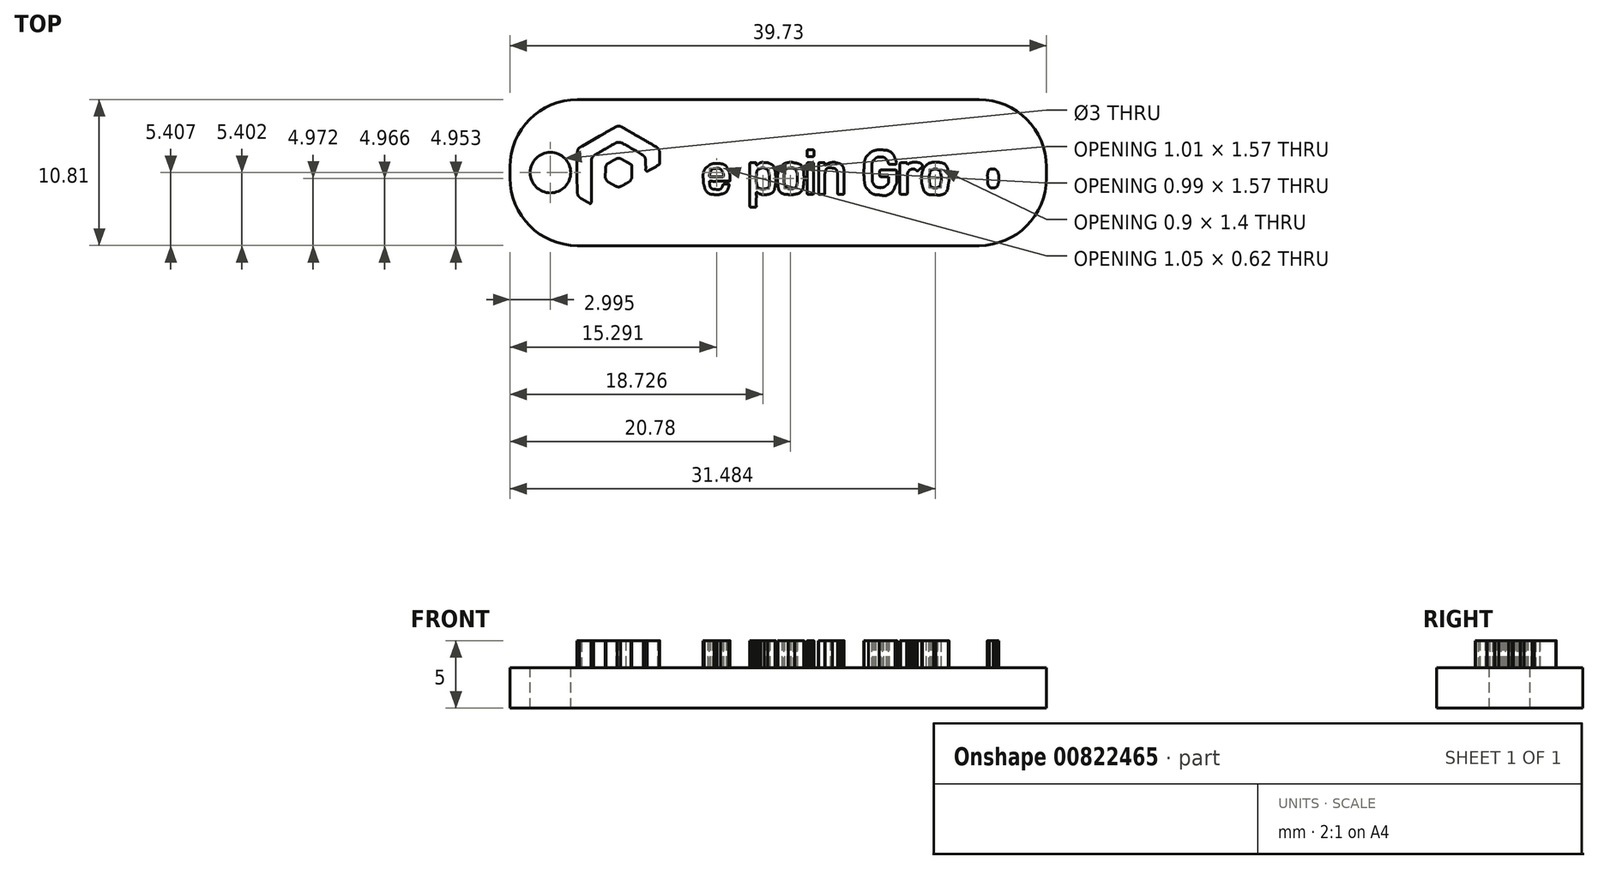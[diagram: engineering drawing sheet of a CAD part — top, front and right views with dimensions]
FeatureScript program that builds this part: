
annotation { "Feature Type Name" : "Feature", "Feature Type Description" : "" }
export const myFeature = defineFeature(function(context is Context, id is Id, definition is map)
    precondition{}
    {
        {
            var Q0;
            Q0=qCreatedBy(makeId("Top.planeOp"),FACE);
            var sketch = newSketch(context, id + "F0", { "sketchPlane" : qUnion([Q0])});
            skFitSpline(sketch, "E0", {"points": [v(-12.93, -3.42) * mm, v(-13.02, -3.4) * mm, v(-12.98, -3.42) * mm, v(-13.42, -3.17) * mm]});
            skFitSpline(sketch, "E1", {"points": [v(-13.42, -3.17) * mm, v(-13.69, -3.02) * mm, v(-13.79, -2.96) * mm, v(-13.8, -2.93) * mm]});
            skFitSpline(sketch, "E2", {"points": [v(-13.8, -2.93) * mm, v(-13.8, -2.9) * mm, v(-13.81, -2.8) * mm, v(-13.81, -2.4) * mm]});
            skFitSpline(sketch, "E3", {"points": [v(-13.81, -2.4) * mm, v(-13.81, -1.9) * mm, v(-13.81, -1.88) * mm, v(-13.77, -1.85) * mm]});
            skFitSpline(sketch, "E4", {"points": [v(-13.77, -1.85) * mm, v(-13.72, -1.82) * mm, v(-13.68, -1.83) * mm, v(-13.36, -2.02) * mm]});
            skFitSpline(sketch, "E5", {"points": [v(-13.36, -2.02) * mm, v(-13.19, -2.12) * mm, v(-13.02, -2.2) * mm, v(-12.98, -2.22) * mm]});
            skFitSpline(sketch, "E6", {"points": [v(-12.98, -2.22) * mm, v(-12.9, -2.25) * mm, v(-12.78, -2.25) * mm, v(-12.7, -2.23) * mm]});
            skFitSpline(sketch, "E7", {"points": [v(-12.7, -2.23) * mm, v(-12.65, -2.21) * mm, v(-12.17, -1.94) * mm, v(-11.38, -1.48) * mm]});
            skFitSpline(sketch, "E8", {"points": [v(-11.38, -1.48) * mm, v(-9.77, -0.55) * mm, v(-9.91, -0.63) * mm, v(-9.87, -0.64) * mm]});
            skFitSpline(sketch, "E9", {"points": [v(-9.87, -0.64) * mm, v(-9.85, -0.65) * mm, v(-9.82, -0.66) * mm, v(-9.81, -0.68) * mm]});
            skFitSpline(sketch, "E10", {"points": [v(-9.81, -0.68) * mm, v(-9.8, -0.7) * mm, v(-9.79, -0.72) * mm, v(-9.79, -1.13) * mm]});
            skFitSpline(sketch, "E11", {"points": [v(-9.79, -1.13) * mm, v(-9.79, -1.5) * mm, v(-9.8, -1.55) * mm, v(-9.81, -1.61) * mm]});
            skFitSpline(sketch, "E12", {"points": [v(-9.81, -1.61) * mm, v(-9.84, -1.7) * mm, v(-9.88, -1.77) * mm, v(-9.95, -1.84) * mm]});
            skFitSpline(sketch, "E13", {"points": [v(-9.95, -1.84) * mm, v(-10.01, -1.9) * mm, v(-12.57, -3.37) * mm, v(-12.66, -3.4) * mm]});
            skFitSpline(sketch, "E14", {"points": [v(-12.66, -3.4) * mm, v(-12.74, -3.43) * mm, v(-12.85, -3.44) * mm, v(-12.93, -3.42) * mm]});
            skFitSpline(sketch, "E15", {"points": [v(-3.1, -2.53) * mm, v(-3.1, -2.5) * mm, v(-3.11, -2.34) * mm, v(-3.11, -0.91) * mm]});
            skFitSpline(sketch, "E16", {"points": [v(-3.11, -0.91) * mm, v(-3.11, 0.5) * mm, v(-3.1, 0.68) * mm, v(-3.1, 0.7) * mm]});
            skFitSpline(sketch, "E17", {"points": [v(-3.1, 0.7) * mm, v(-3.08, 0.73) * mm, v(-3.07, 0.73) * mm, v(-2.88, 0.73) * mm]});
            skFitSpline(sketch, "E18", {"points": [v(-2.88, 0.73) * mm, v(-2.65, 0.73) * mm, v(-2.64, 0.73) * mm, v(-2.64, 0.63) * mm]});
            skFitSpline(sketch, "E19", {"points": [v(-2.64, 0.63) * mm, v(-2.64, 0.59) * mm, v(-2.63, 0.58) * mm, v(-2.6, 0.57) * mm]});
            skFitSpline(sketch, "E20", {"points": [v(-2.6, 0.57) * mm, v(-2.58, 0.56) * mm, v(-2.57, 0.57) * mm, v(-2.5, 0.61) * mm]});
            skFitSpline(sketch, "E21", {"points": [v(-2.5, 0.61) * mm, v(-2.36, 0.72) * mm, v(-2.22, 0.76) * mm, v(-1.99, 0.75) * mm]});
            skFitSpline(sketch, "E22", {"points": [v(-1.99, 0.75) * mm, v(-1.82, 0.74) * mm, v(-1.75, 0.73) * mm, v(-1.62, 0.67) * mm]});
            skFitSpline(sketch, "E23", {"points": [v(-1.62, 0.67) * mm, v(-1.46, 0.59) * mm, v(-1.33, 0.41) * mm, v(-1.26, 0.2) * mm]});
            skFitSpline(sketch, "E24", {"points": [v(-1.26, 0.2) * mm, v(-1.22, 0.05) * mm, v(-1.2, -0.06) * mm, v(-1.2, -0.36) * mm]});
            skFitSpline(sketch, "E25", {"points": [v(-1.2, -0.36) * mm, v(-1.2, -0.68) * mm, v(-1.2, -0.84) * mm, v(-1.25, -1.02) * mm]});
            skFitSpline(sketch, "E26", {"points": [v(-1.25, -1.02) * mm, v(-1.32, -1.34) * mm, v(-1.5, -1.53) * mm, v(-1.78, -1.6) * mm]});
            skFitSpline(sketch, "E27", {"points": [v(-1.78, -1.6) * mm, v(-1.83, -1.62) * mm, v(-1.9, -1.63) * mm, v(-2.03, -1.63) * mm]});
            skFitSpline(sketch, "E28", {"points": [v(-2.03, -1.63) * mm, v(-2.19, -1.63) * mm, v(-2.22, -1.63) * mm, v(-2.3, -1.6) * mm]});
            skFitSpline(sketch, "E29", {"points": [v(-2.3, -1.6) * mm, v(-2.38, -1.58) * mm, v(-2.45, -1.54) * mm, v(-2.52, -1.49) * mm]});
            skFitSpline(sketch, "E30", {"points": [v(-2.52, -1.49) * mm, v(-2.56, -1.45) * mm, v(-2.6, -1.45) * mm, v(-2.62, -1.47) * mm]});
            skFitSpline(sketch, "E31", {"points": [v(-2.62, -1.47) * mm, v(-2.63, -1.48) * mm, v(-2.63, -1.61) * mm, v(-2.63, -2) * mm]});
            skFitSpline(sketch, "E32", {"points": [v(-2.63, -2) * mm, v(-2.63, -2.44) * mm, v(-2.63, -2.5) * mm, v(-2.65, -2.53) * mm]});
            skFitSpline(sketch, "E33", {"points": [v(-2.65, -2.53) * mm, v(-2.66, -2.55) * mm, v(-2.67, -2.55) * mm, v(-2.87, -2.55) * mm]});
            skFitSpline(sketch, "E34", {"points": [v(-2.87, -2.55) * mm, v(-3.07, -2.55) * mm, v(-3.08, -2.55) * mm, v(-3.1, -2.53) * mm]});
            skFitSpline(sketch, "E35", {"points": [v(-2, -1.2) * mm, v(-1.75, -1.12) * mm, v(-1.65, -0.87) * mm, v(-1.67, -0.35) * mm]});
            skFitSpline(sketch, "E36", {"points": [v(-1.67, -0.35) * mm, v(-1.68, -0.14) * mm, v(-1.7, -0.02) * mm, v(-1.75, 0.1) * mm]});
            skFitSpline(sketch, "E37", {"points": [v(-1.75, 0.1) * mm, v(-1.79, 0.18) * mm, v(-1.86, 0.26) * mm, v(-1.94, 0.3) * mm]});
            skFitSpline(sketch, "E38", {"points": [v(-1.94, 0.3) * mm, v(-2.05, 0.34) * mm, v(-2.24, 0.34) * mm, v(-2.36, 0.3) * mm]});
            skFitSpline(sketch, "E39", {"points": [v(-2.36, 0.3) * mm, v(-2.5, 0.23) * mm, v(-2.59, 0.08) * mm, v(-2.62, -0.17) * mm]});
            skFitSpline(sketch, "E40", {"points": [v(-2.62, -0.17) * mm, v(-2.64, -0.32) * mm, v(-2.63, -0.71) * mm, v(-2.6, -0.82) * mm]});
            skFitSpline(sketch, "E41", {"points": [v(-2.6, -0.82) * mm, v(-2.56, -1.01) * mm, v(-2.46, -1.14) * mm, v(-2.32, -1.19) * mm]});
            skFitSpline(sketch, "E42", {"points": [v(-2.32, -1.19) * mm, v(-2.24, -1.21) * mm, v(-2.08, -1.22) * mm, v(-2, -1.2) * mm]});
            skFitSpline(sketch, "E43", {"points": [v(13.97, -2.53) * mm, v(13.96, -2.52) * mm, v(13.94, -2.5) * mm, v(13.93, -2.49) * mm]});
            skFitSpline(sketch, "E44", {"points": [v(13.93, -2.49) * mm, v(13.91, -2.46) * mm, v(13.9, -2.33) * mm, v(13.9, -0.9) * mm]});
            skFitSpline(sketch, "E45", {"points": [v(13.9, -0.9) * mm, v(13.9, 0.8) * mm, v(13.9, 0.7) * mm, v(13.97, 0.74) * mm]});
            skFitSpline(sketch, "E46", {"points": [v(13.97, 0.74) * mm, v(13.99, 0.75) * mm, v(14.07, 0.75) * mm, v(14.2, 0.75) * mm]});
            skFitSpline(sketch, "E47", {"points": [v(14.44, 0.72) * mm, v(14.46, 0.7) * mm, v(14.47, 0.68) * mm, v(14.47, 0.64) * mm]});
            skLineSegment(sketch, "E48", {"start": v(14.2, 0.75) * mm, "end": v(14.4, 0.75) * mm});
            skLineSegment(sketch, "E49", {"start": v(14.4, 0.75) * mm, "end": v(14.44, 0.72) * mm});
            skFitSpline(sketch, "E50", {"points": [v(14.52, 0.63) * mm, v(14.6, 0.69) * mm, v(14.68, 0.73) * mm, v(14.79, 0.75) * mm]});
            skFitSpline(sketch, "E51", {"points": [v(14.79, 0.75) * mm, v(14.91, 0.78) * mm, v(15.17, 0.78) * mm, v(15.3, 0.74) * mm]});
            skFitSpline(sketch, "E52", {"points": [v(15.3, 0.74) * mm, v(15.63, 0.63) * mm, v(15.8, 0.4) * mm, v(15.86, -0.05) * mm]});
            skFitSpline(sketch, "E53", {"points": [v(15.86, -0.05) * mm, v(15.88, -0.2) * mm, v(15.88, -0.7) * mm, v(15.86, -0.86) * mm]});
            skFitSpline(sketch, "E54", {"points": [v(15.86, -0.86) * mm, v(15.79, -1.3) * mm, v(15.6, -1.53) * mm, v(15.26, -1.63) * mm]});
            skFitSpline(sketch, "E55", {"points": [v(15.26, -1.63) * mm, v(15.19, -1.64) * mm, v(15.14, -1.65) * mm, v(15.01, -1.65) * mm]});
            skFitSpline(sketch, "E56", {"points": [v(15.01, -1.65) * mm, v(14.8, -1.65) * mm, v(14.67, -1.62) * mm, v(14.53, -1.52) * mm]});
            skLineSegment(sketch, "E57", {"start": v(14.47, 0.64) * mm, "end": v(14.47, 0.6) * mm});
            skLineSegment(sketch, "E58", {"start": v(14.47, 0.6) * mm, "end": v(14.52, 0.63) * mm});
            skFitSpline(sketch, "E59", {"points": [v(14.48, -1.97) * mm, v(14.48, -2.5) * mm, v(14.48, -2.5) * mm, v(14.42, -2.53) * mm]});
            skFitSpline(sketch, "E60", {"points": [v(14.42, -2.53) * mm, v(14.38, -2.55) * mm, v(14, -2.55) * mm, v(13.97, -2.53) * mm]});
            skLineSegment(sketch, "E61", {"start": v(14.53, -1.52) * mm, "end": v(14.48, -1.48) * mm});
            skLineSegment(sketch, "E62", {"start": v(14.48, -1.48) * mm, "end": v(14.48, -1.97) * mm});
            skFitSpline(sketch, "E63", {"points": [v(15.08, -1.1) * mm, v(15.18, -1.06) * mm, v(15.24, -0.97) * mm, v(15.28, -0.8) * mm]});
            skFitSpline(sketch, "E64", {"points": [v(15.28, -0.8) * mm, v(15.31, -0.7) * mm, v(15.31, -0.17) * mm, v(15.28, -0.07) * mm]});
            skFitSpline(sketch, "E65", {"points": [v(15.28, -0.07) * mm, v(15.25, 0.05) * mm, v(15.22, 0.1) * mm, v(15.16, 0.17) * mm]});
            skFitSpline(sketch, "E66", {"points": [v(15.16, 0.17) * mm, v(15.08, 0.24) * mm, v(15, 0.26) * mm, v(14.87, 0.26) * mm]});
            skFitSpline(sketch, "E67", {"points": [v(14.87, 0.26) * mm, v(14.67, 0.25) * mm, v(14.56, 0.15) * mm, v(14.5, -0.07) * mm]});
            skFitSpline(sketch, "E68", {"points": [v(14.5, -0.07) * mm, v(14.49, -0.14) * mm, v(14.49, -0.2) * mm, v(14.49, -0.44) * mm]});
            skFitSpline(sketch, "E69", {"points": [v(14.49, -0.44) * mm, v(14.49, -0.7) * mm, v(14.49, -0.74) * mm, v(14.51, -0.82) * mm]});
            skFitSpline(sketch, "E70", {"points": [v(14.51, -0.82) * mm, v(14.54, -0.93) * mm, v(14.58, -1) * mm, v(14.64, -1.05) * mm]});
            skFitSpline(sketch, "E71", {"points": [v(14.64, -1.05) * mm, v(14.71, -1.11) * mm, v(14.78, -1.13) * mm, v(14.91, -1.13) * mm]});
            skFitSpline(sketch, "E72", {"points": [v(14.91, -1.13) * mm, v(15, -1.13) * mm, v(15.04, -1.12) * mm, v(15.07, -1.1) * mm]});
            skFitSpline(sketch, "E73", {"points": [v(-15.32, -2.08) * mm, v(-15.58, -1.93) * mm, v(-15.67, -1.87) * mm, v(-15.72, -1.82) * mm]});
            skFitSpline(sketch, "E74", {"points": [v(-15.72, -1.82) * mm, v(-15.8, -1.75) * mm, v(-15.84, -1.67) * mm, v(-15.86, -1.57) * mm]});
            skFitSpline(sketch, "E75", {"points": [v(-15.86, -1.57) * mm, v(-15.88, -1.49) * mm, v(-15.88, 1.49) * mm, v(-15.86, 1.57) * mm]});
            skFitSpline(sketch, "E76", {"points": [v(-15.86, 1.57) * mm, v(-15.83, 1.73) * mm, v(-15.74, 1.84) * mm, v(-15.53, 1.95) * mm]});
            skFitSpline(sketch, "E77", {"points": [v(-15.53, 1.95) * mm, v(-15.46, 2) * mm, v(-14.87, 2.34) * mm, v(-14.22, 2.71) * mm]});
            skFitSpline(sketch, "E78", {"points": [v(-14.22, 2.71) * mm, v(-13.57, 3.08) * mm, v(-13.02, 3.4) * mm, v(-12.98, 3.41) * mm]});
            skFitSpline(sketch, "E79", {"points": [v(-12.98, 3.41) * mm, v(-12.9, 3.44) * mm, v(-12.75, 3.44) * mm, v(-12.67, 3.4) * mm]});
            skFitSpline(sketch, "E80", {"points": [v(-12.67, 3.4) * mm, v(-12.63, 3.4) * mm, v(-12.02, 3.05) * mm, v(-11.3, 2.64) * mm]});
            skFitSpline(sketch, "E81", {"points": [v(-11.3, 2.64) * mm, v(-10.33, 2.07) * mm, v(-10, 1.87) * mm, v(-9.94, 1.83) * mm]});
            skFitSpline(sketch, "E82", {"points": [v(-9.94, 1.83) * mm, v(-9.9, 1.79) * mm, v(-9.87, 1.74) * mm, v(-9.84, 1.68) * mm]});
            skFitSpline(sketch, "E83", {"points": [v(-9.8, 1.12) * mm, v(-9.79, 0.67) * mm, v(-9.79, 0.64) * mm, v(-9.8, 0.62) * mm]});
            skFitSpline(sketch, "E84", {"points": [v(-9.8, 0.62) * mm, v(-9.84, 0.6) * mm, v(-10.69, 0.1) * mm, v(-10.71, 0.1) * mm]});
            skFitSpline(sketch, "E85", {"points": [v(-10.71, 0.1) * mm, v(-10.75, 0.1) * mm, v(-10.79, 0.13) * mm, v(-10.8, 0.16) * mm]});
            skFitSpline(sketch, "E86", {"points": [v(-10.8, 0.16) * mm, v(-10.82, 0.18) * mm, v(-10.82, 0.26) * mm, v(-10.82, 0.57) * mm]});
            skFitSpline(sketch, "E87", {"points": [v(-10.82, 0.57) * mm, v(-10.82, 0.91) * mm, v(-10.82, 0.96) * mm, v(-10.84, 1.02) * mm]});
            skFitSpline(sketch, "E88", {"points": [v(-10.84, 1.02) * mm, v(-10.87, 1.1) * mm, v(-10.92, 1.19) * mm, v(-10.98, 1.24) * mm]});
            skFitSpline(sketch, "E89", {"points": [v(-10.98, 1.24) * mm, v(-11.06, 1.3) * mm, v(-12.62, 2.2) * mm, v(-12.7, 2.23) * mm]});
            skFitSpline(sketch, "E90", {"points": [v(-12.7, 2.23) * mm, v(-12.74, 2.24) * mm, v(-12.8, 2.24) * mm, v(-12.86, 2.24) * mm]});
            skFitSpline(sketch, "E91", {"points": [v(-12.86, 2.24) * mm, v(-12.94, 2.24) * mm, v(-12.97, 2.23) * mm, v(-13.04, 2.2) * mm]});
            skFitSpline(sketch, "E92", {"points": [v(-13.04, 2.2) * mm, v(-13.09, 2.17) * mm, v(-13.46, 1.96) * mm, v(-13.88, 1.72) * mm]});
            skFitSpline(sketch, "E93", {"points": [v(-13.88, 1.72) * mm, v(-14.46, 1.38) * mm, v(-14.65, 1.27) * mm, v(-14.7, 1.22) * mm]});
            skFitSpline(sketch, "E94", {"points": [v(-14.7, 1.22) * mm, v(-14.76, 1.16) * mm, v(-14.82, 1.06) * mm, v(-14.83, 0.97) * mm]});
            skFitSpline(sketch, "E95", {"points": [v(-14.83, 0.97) * mm, v(-14.84, 0.93) * mm, v(-14.84, 0.34) * mm, v(-14.84, -0.66) * mm]});
            skLineSegment(sketch, "E96", {"start": v(-9.84, 1.68) * mm, "end": v(-9.8, 1.6) * mm});
            skLineSegment(sketch, "E97", {"start": v(-9.8, 1.6) * mm, "end": v(-9.8, 1.12) * mm});
            skFitSpline(sketch, "E98", {"points": [v(-14.87, -2.25) * mm, v(-14.93, -2.3) * mm, v(-14.95, -2.3) * mm, v(-15.32, -2.08) * mm]});
            skLineSegment(sketch, "E99", {"start": v(-14.84, -0.66) * mm, "end": v(-14.84, -2.22) * mm});
            skLineSegment(sketch, "E100", {"start": v(-14.84, -2.22) * mm, "end": v(-14.87, -2.25) * mm});
            skFitSpline(sketch, "E101", {"points": [v(6.45, -1.65) * mm, v(6.13, -1.62) * mm, v(5.88, -1.5) * mm, v(5.67, -1.3) * mm]});
            skFitSpline(sketch, "E102", {"points": [v(5.67, -1.3) * mm, v(5.5, -1.1) * mm, v(5.4, -0.9) * mm, v(5.37, -0.6) * mm]});
            skFitSpline(sketch, "E103", {"points": [v(5.37, -0.6) * mm, v(5.35, -0.43) * mm, v(5.35, 0.46) * mm, v(5.37, 0.63) * mm]});
            skFitSpline(sketch, "E104", {"points": [v(5.37, 0.63) * mm, v(5.4, 0.95) * mm, v(5.5, 1.17) * mm, v(5.7, 1.36) * mm]});
            skFitSpline(sketch, "E105", {"points": [v(5.7, 1.36) * mm, v(5.84, 1.5) * mm, v(6.01, 1.6) * mm, v(6.22, 1.65) * mm]});
            skFitSpline(sketch, "E106", {"points": [v(6.22, 1.65) * mm, v(6.37, 1.7) * mm, v(6.62, 1.7) * mm, v(6.78, 1.68) * mm]});
            skFitSpline(sketch, "E107", {"points": [v(6.78, 1.68) * mm, v(7.18, 1.6) * mm, v(7.47, 1.4) * mm, v(7.64, 1.05) * mm]});
            skFitSpline(sketch, "E108", {"points": [v(7.64, 1.05) * mm, v(7.67, 0.98) * mm, v(7.71, 0.88) * mm, v(7.73, 0.82) * mm]});
            skFitSpline(sketch, "E109", {"points": [v(7.73, 0.82) * mm, v(7.76, 0.72) * mm, v(7.76, 0.7) * mm, v(7.74, 0.67) * mm]});
            skFitSpline(sketch, "E110", {"points": [v(7.74, 0.67) * mm, v(7.73, 0.65) * mm, v(7.72, 0.62) * mm, v(7.7, 0.62) * mm]});
            skFitSpline(sketch, "E111", {"points": [v(7.7, 0.62) * mm, v(7.69, 0.61) * mm, v(7.6, 0.6) * mm, v(7.45, 0.6) * mm]});
            skFitSpline(sketch, "E112", {"points": [v(7.45, 0.6) * mm, v(7.27, 0.6) * mm, v(7.22, 0.6) * mm, v(7.2, 0.62) * mm]});
            skFitSpline(sketch, "E113", {"points": [v(7.2, 0.62) * mm, v(7.19, 0.63) * mm, v(7.16, 0.68) * mm, v(7.15, 0.73) * mm]});
            skFitSpline(sketch, "E114", {"points": [v(7.15, 0.73) * mm, v(7.1, 0.84) * mm, v(7.05, 0.92) * mm, v(6.98, 1) * mm]});
            skFitSpline(sketch, "E115", {"points": [v(6.98, 1) * mm, v(6.86, 1.11) * mm, v(6.7, 1.16) * mm, v(6.52, 1.15) * mm]});
            skFitSpline(sketch, "E116", {"points": [v(6.52, 1.15) * mm, v(6.36, 1.14) * mm, v(6.24, 1.09) * mm, v(6.13, 0.99) * mm]});
            skFitSpline(sketch, "E117", {"points": [v(6.13, 0.99) * mm, v(5.98, 0.83) * mm, v(5.93, 0.58) * mm, v(5.95, -0.1) * mm]});
            skFitSpline(sketch, "E118", {"points": [v(5.95, -0.1) * mm, v(5.95, -0.56) * mm, v(5.97, -0.69) * mm, v(6.06, -0.85) * mm]});
            skFitSpline(sketch, "E119", {"points": [v(6.06, -0.85) * mm, v(6.12, -0.96) * mm, v(6.25, -1.06) * mm, v(6.4, -1.1) * mm]});
            skFitSpline(sketch, "E120", {"points": [v(6.4, -1.1) * mm, v(6.46, -1.11) * mm, v(6.62, -1.11) * mm, v(6.7, -1.1) * mm]});
            skFitSpline(sketch, "E121", {"points": [v(6.7, -1.1) * mm, v(6.8, -1.08) * mm, v(6.93, -1.01) * mm, v(7, -0.94) * mm]});
            skFitSpline(sketch, "E122", {"points": [v(7, -0.94) * mm, v(7.13, -0.8) * mm, v(7.17, -0.67) * mm, v(7.17, -0.45) * mm]});
            skFitSpline(sketch, "E123", {"points": [v(7.77, -0.2) * mm, v(7.77, -0.67) * mm, v(7.75, -0.8) * mm, v(7.64, -1.02) * mm]});
            skFitSpline(sketch, "E124", {"points": [v(7.64, -1.02) * mm, v(7.44, -1.44) * mm, v(6.97, -1.7) * mm, v(6.45, -1.65) * mm]});
            skLineSegment(sketch, "E125", {"start": v(7.17, -0.45) * mm, "end": v(7.17, -0.31) * mm});
            skLineSegment(sketch, "E126", {"start": v(7.17, -0.31) * mm, "end": v(6.87, -0.31) * mm});
            skLineSegment(sketch, "E127", {"start": v(6.87, -0.31) * mm, "end": v(6.57, -0.31) * mm});
            skLineSegment(sketch, "E128", {"start": v(6.57, -0.31) * mm, "end": v(6.54, -0.28) * mm});
            skLineSegment(sketch, "E129", {"start": v(6.54, -0.28) * mm, "end": v(6.5, -0.26) * mm});
            skLineSegment(sketch, "E130", {"start": v(6.5, -0.26) * mm, "end": v(6.5, -0.06) * mm});
            skLineSegment(sketch, "E131", {"start": v(6.5, -0.06) * mm, "end": v(6.5, 0.14) * mm});
            skLineSegment(sketch, "E132", {"start": v(6.5, 0.14) * mm, "end": v(6.53, 0.17) * mm});
            skLineSegment(sketch, "E133", {"start": v(6.53, 0.17) * mm, "end": v(6.56, 0.2) * mm});
            skLineSegment(sketch, "E134", {"start": v(6.56, 0.2) * mm, "end": v(7.14, 0.2) * mm});
            skLineSegment(sketch, "E135", {"start": v(7.14, 0.2) * mm, "end": v(7.7, 0.2) * mm});
            skLineSegment(sketch, "E136", {"start": v(7.7, 0.2) * mm, "end": v(7.74, 0.17) * mm});
            skLineSegment(sketch, "E137", {"start": v(7.74, 0.17) * mm, "end": v(7.77, 0.14) * mm});
            skLineSegment(sketch, "E138", {"start": v(7.77, 0.14) * mm, "end": v(7.77, -0.2) * mm});
            skFitSpline(sketch, "E139", {"points": [v(10.49, -1.65) * mm, v(10.09, -1.6) * mm, v(9.8, -1.36) * mm, v(9.68, -0.99) * mm]});
            skFitSpline(sketch, "E140", {"points": [v(9.68, -0.99) * mm, v(9.63, -0.83) * mm, v(9.61, -0.66) * mm, v(9.62, -0.37) * mm]});
            skFitSpline(sketch, "E141", {"points": [v(9.62, -0.37) * mm, v(9.63, -0.1) * mm, v(9.64, 0.02) * mm, v(9.7, 0.17) * mm]});
            skFitSpline(sketch, "E142", {"points": [v(9.7, 0.17) * mm, v(9.75, 0.31) * mm, v(9.8, 0.39) * mm, v(9.91, 0.5) * mm]});
            skFitSpline(sketch, "E143", {"points": [v(9.91, 0.5) * mm, v(10.05, 0.63) * mm, v(10.16, 0.7) * mm, v(10.34, 0.75) * mm]});
            skFitSpline(sketch, "E144", {"points": [v(10.34, 0.75) * mm, v(10.43, 0.77) * mm, v(10.7, 0.78) * mm, v(10.8, 0.76) * mm]});
            skFitSpline(sketch, "E145", {"points": [v(10.8, 0.76) * mm, v(11.2, 0.7) * mm, v(11.49, 0.42) * mm, v(11.58, 0) * mm]});
            skFitSpline(sketch, "E146", {"points": [v(11.58, 0) * mm, v(11.63, -0.21) * mm, v(11.63, -0.66) * mm, v(11.58, -0.88) * mm]});
            skFitSpline(sketch, "E147", {"points": [v(11.58, -0.88) * mm, v(11.48, -1.35) * mm, v(11.15, -1.62) * mm, v(10.66, -1.65) * mm]});
            skFitSpline(sketch, "E148", {"points": [v(10.66, -1.65) * mm, v(10.6, -1.65) * mm, v(10.53, -1.65) * mm, v(10.49, -1.65) * mm]});
            skFitSpline(sketch, "E149", {"points": [v(10.8, -1.1) * mm, v(10.91, -1.04) * mm, v(10.98, -0.95) * mm, v(11.03, -0.78) * mm]});
            skFitSpline(sketch, "E150", {"points": [v(11.03, -0.78) * mm, v(11.05, -0.67) * mm, v(11.05, -0.2) * mm, v(11.03, -0.1) * mm]});
            skFitSpline(sketch, "E151", {"points": [v(11.03, -0.1) * mm, v(10.98, 0.07) * mm, v(10.92, 0.17) * mm, v(10.8, 0.22) * mm]});
            skFitSpline(sketch, "E152", {"points": [v(10.8, 0.22) * mm, v(10.74, 0.25) * mm, v(10.72, 0.25) * mm, v(10.61, 0.25) * mm]});
            skFitSpline(sketch, "E153", {"points": [v(10.61, 0.25) * mm, v(10.51, 0.25) * mm, v(10.49, 0.25) * mm, v(10.43, 0.22) * mm]});
            skFitSpline(sketch, "E154", {"points": [v(10.43, 0.22) * mm, v(10.32, 0.17) * mm, v(10.25, 0.07) * mm, v(10.21, -0.07) * mm]});
            skFitSpline(sketch, "E155", {"points": [v(10.21, -0.07) * mm, v(10.18, -0.22) * mm, v(10.17, -0.58) * mm, v(10.2, -0.76) * mm]});
            skFitSpline(sketch, "E156", {"points": [v(10.2, -0.76) * mm, v(10.24, -0.93) * mm, v(10.33, -1.06) * mm, v(10.46, -1.1) * mm]});
            skFitSpline(sketch, "E157", {"points": [v(10.46, -1.1) * mm, v(10.55, -1.14) * mm, v(10.7, -1.14) * mm, v(10.8, -1.1) * mm]});
            skFitSpline(sketch, "E158", {"points": [v(12.5, -1.65) * mm, v(12.3, -1.62) * mm, v(12.15, -1.55) * mm, v(12.02, -1.42) * mm]});
            skFitSpline(sketch, "E159", {"points": [v(12.02, -1.42) * mm, v(11.89, -1.28) * mm, v(11.82, -1.13) * mm, v(11.8, -0.92) * mm]});
            skFitSpline(sketch, "E160", {"points": [v(11.8, -0.92) * mm, v(11.78, -0.86) * mm, v(11.78, -0.52) * mm, v(11.78, -0.08) * mm]});
            skFitSpline(sketch, "E161", {"points": [v(11.78, -0.08) * mm, v(11.78, 0.73) * mm, v(11.78, 0.7) * mm, v(11.84, 0.74) * mm]});
            skFitSpline(sketch, "E162", {"points": [v(11.84, 0.74) * mm, v(11.86, 0.75) * mm, v(11.94, 0.75) * mm, v(12.07, 0.75) * mm]});
            skFitSpline(sketch, "E163", {"points": [v(12.07, 0.75) * mm, v(12.27, 0.75) * mm, v(12.31, 0.74) * mm, v(12.34, 0.7) * mm]});
            skFitSpline(sketch, "E164", {"points": [v(12.34, 0.7) * mm, v(12.34, 0.69) * mm, v(12.35, 0.34) * mm, v(12.35, -0.08) * mm]});
            skFitSpline(sketch, "E165", {"points": [v(12.38, -0.9) * mm, v(12.42, -0.98) * mm, v(12.48, -1.06) * mm, v(12.56, -1.1) * mm]});
            skFitSpline(sketch, "E166", {"points": [v(12.56, -1.1) * mm, v(12.61, -1.12) * mm, v(12.63, -1.13) * mm, v(12.75, -1.13) * mm]});
            skFitSpline(sketch, "E167", {"points": [v(12.75, -1.13) * mm, v(12.87, -1.13) * mm, v(12.89, -1.12) * mm, v(12.95, -1.1) * mm]});
            skFitSpline(sketch, "E168", {"points": [v(12.95, -1.1) * mm, v(13.03, -1.06) * mm, v(13.1, -0.98) * mm, v(13.13, -0.9) * mm]});
            skFitSpline(sketch, "E169", {"points": [v(13.13, -0.9) * mm, v(13.15, -0.83) * mm, v(13.15, -0.83) * mm, v(13.16, -0.07) * mm]});
            skLineSegment(sketch, "E170", {"start": v(12.35, -0.08) * mm, "end": v(12.36, -0.83) * mm});
            skLineSegment(sketch, "E171", {"start": v(12.36, -0.83) * mm, "end": v(12.38, -0.9) * mm});
            skFitSpline(sketch, "E172", {"points": [v(13.45, -1.62) * mm, v(13.24, -1.62) * mm, v(13.24, -1.62) * mm, v(13.21, -1.6) * mm]});
            skFitSpline(sketch, "E173", {"points": [v(13.21, -1.6) * mm, v(13.2, -1.58) * mm, v(13.18, -1.55) * mm, v(13.17, -1.52) * mm]});
            skLineSegment(sketch, "E174", {"start": v(13.16, -0.07) * mm, "end": v(13.16, 0.69) * mm});
            skLineSegment(sketch, "E175", {"start": v(13.16, 0.69) * mm, "end": v(13.2, 0.72) * mm});
            skLineSegment(sketch, "E176", {"start": v(13.2, 0.72) * mm, "end": v(13.24, 0.75) * mm});
            skLineSegment(sketch, "E177", {"start": v(13.24, 0.75) * mm, "end": v(13.45, 0.75) * mm});
            skLineSegment(sketch, "E178", {"start": v(13.45, 0.75) * mm, "end": v(13.66, 0.75) * mm});
            skLineSegment(sketch, "E179", {"start": v(13.66, 0.75) * mm, "end": v(13.7, 0.72) * mm});
            skLineSegment(sketch, "E180", {"start": v(13.7, 0.72) * mm, "end": v(13.73, 0.69) * mm});
            skLineSegment(sketch, "E181", {"start": v(13.73, 0.69) * mm, "end": v(13.73, -0.44) * mm});
            skLineSegment(sketch, "E182", {"start": v(13.73, -0.44) * mm, "end": v(13.73, -1.56) * mm});
            skLineSegment(sketch, "E183", {"start": v(13.73, -1.56) * mm, "end": v(13.7, -1.6) * mm});
            skLineSegment(sketch, "E184", {"start": v(13.7, -1.6) * mm, "end": v(13.66, -1.62) * mm});
            skLineSegment(sketch, "E185", {"start": v(13.66, -1.62) * mm, "end": v(13.45, -1.62) * mm});
            skFitSpline(sketch, "E186", {"points": [v(13.13, -1.5) * mm, v(12.96, -1.61) * mm, v(12.71, -1.67) * mm, v(12.5, -1.65) * mm]});
            skLineSegment(sketch, "E187", {"start": v(13.17, -1.52) * mm, "end": v(13.17, -1.48) * mm});
            skLineSegment(sketch, "E188", {"start": v(13.17, -1.48) * mm, "end": v(13.13, -1.5) * mm});
            skFitSpline(sketch, "E189", {"points": [v(-5.76, -1.62) * mm, v(-6.11, -1.56) * mm, v(-6.37, -1.33) * mm, v(-6.49, -0.96) * mm]});
            skFitSpline(sketch, "E190", {"points": [v(-6.49, -0.96) * mm, v(-6.54, -0.8) * mm, v(-6.56, -0.66) * mm, v(-6.56, -0.47) * mm]});
            skFitSpline(sketch, "E191", {"points": [v(-6.56, -0.47) * mm, v(-6.56, -0.07) * mm, v(-6.45, 0.25) * mm, v(-6.22, 0.46) * mm]});
            skFitSpline(sketch, "E192", {"points": [v(-6.22, 0.46) * mm, v(-6.12, 0.55) * mm, v(-6.03, 0.6) * mm, v(-5.9, 0.65) * mm]});
            skFitSpline(sketch, "E193", {"points": [v(-5.9, 0.65) * mm, v(-5.79, 0.69) * mm, v(-5.78, 0.69) * mm, v(-5.57, 0.69) * mm]});
            skFitSpline(sketch, "E194", {"points": [v(-5.57, 0.69) * mm, v(-5.38, 0.69) * mm, v(-5.35, 0.69) * mm, v(-5.27, 0.66) * mm]});
            skFitSpline(sketch, "E195", {"points": [v(-5.27, 0.66) * mm, v(-5.02, 0.6) * mm, v(-4.84, 0.44) * mm, v(-4.72, 0.2) * mm]});
            skFitSpline(sketch, "E196", {"points": [v(-4.72, 0.2) * mm, v(-4.64, 0.02) * mm, v(-4.6, -0.17) * mm, v(-4.58, -0.43) * mm]});
            skFitSpline(sketch, "E197", {"points": [v(-4.58, -0.43) * mm, v(-4.58, -0.6) * mm, v(-4.58, -0.6) * mm, v(-4.6, -0.62) * mm]});
            skFitSpline(sketch, "E198", {"points": [v(-4.6, -0.62) * mm, v(-4.63, -0.64) * mm, v(-4.7, -0.64) * mm, v(-5.35, -0.64) * mm]});
            skFitSpline(sketch, "E199", {"points": [v(-5.35, -0.64) * mm, v(-5.98, -0.64) * mm, v(-6.07, -0.64) * mm, v(-6.08, -0.66) * mm]});
            skFitSpline(sketch, "E200", {"points": [v(-6.08, -0.66) * mm, v(-6.1, -0.67) * mm, v(-6.1, -0.7) * mm, v(-6.09, -0.75) * mm]});
            skFitSpline(sketch, "E201", {"points": [v(-6.09, -0.75) * mm, v(-6.06, -1.01) * mm, v(-5.9, -1.2) * mm, v(-5.65, -1.24) * mm]});
            skFitSpline(sketch, "E202", {"points": [v(-5.65, -1.24) * mm, v(-5.42, -1.27) * mm, v(-5.22, -1.16) * mm, v(-5.12, -0.96) * mm]});
            skFitSpline(sketch, "E203", {"points": [v(-5.12, -0.96) * mm, v(-5.1, -0.92) * mm, v(-5.08, -0.87) * mm, v(-5.06, -0.87) * mm]});
            skFitSpline(sketch, "E204", {"points": [v(-5.06, -0.87) * mm, v(-5.05, -0.86) * mm, v(-5, -0.85) * mm, v(-4.86, -0.85) * mm]});
            skFitSpline(sketch, "E205", {"points": [v(-4.86, -0.85) * mm, v(-4.7, -0.85) * mm, v(-4.67, -0.85) * mm, v(-4.65, -0.87) * mm]});
            skFitSpline(sketch, "E206", {"points": [v(-4.65, -0.87) * mm, v(-4.63, -0.9) * mm, v(-4.63, -0.93) * mm, v(-4.66, -1.02) * mm]});
            skFitSpline(sketch, "E207", {"points": [v(-4.66, -1.02) * mm, v(-4.78, -1.32) * mm, v(-4.98, -1.51) * mm, v(-5.27, -1.6) * mm]});
            skFitSpline(sketch, "E208", {"points": [v(-5.27, -1.6) * mm, v(-5.35, -1.62) * mm, v(-5.4, -1.63) * mm, v(-5.54, -1.63) * mm]});
            skFitSpline(sketch, "E209", {"points": [v(-5.54, -1.63) * mm, v(-5.63, -1.63) * mm, v(-5.73, -1.63) * mm, v(-5.76, -1.62) * mm]});
            skFitSpline(sketch, "E210", {"points": [v(-5.07, -0.28) * mm, v(-5.06, -0.26) * mm, v(-5.05, -0.24) * mm, v(-5.06, -0.18) * mm]});
            skFitSpline(sketch, "E211", {"points": [v(-5.06, -0.18) * mm, v(-5.08, -0.08) * mm, v(-5.09, -0.04) * mm, v(-5.14, 0.05) * mm]});
            skFitSpline(sketch, "E212", {"points": [v(-5.14, 0.05) * mm, v(-5.23, 0.22) * mm, v(-5.4, 0.31) * mm, v(-5.61, 0.3) * mm]});
            skFitSpline(sketch, "E213", {"points": [v(-5.61, 0.3) * mm, v(-5.82, 0.29) * mm, v(-5.98, 0.17) * mm, v(-6.05, -0.04) * mm]});
            skFitSpline(sketch, "E214", {"points": [v(-6.05, -0.04) * mm, v(-6.09, -0.13) * mm, v(-6.1, -0.26) * mm, v(-6.08, -0.28) * mm]});
            skFitSpline(sketch, "E215", {"points": [v(-6.08, -0.28) * mm, v(-6.07, -0.3) * mm, v(-6, -0.3) * mm, v(-5.58, -0.3) * mm]});
            skFitSpline(sketch, "E216", {"points": [v(-0.27, -1.62) * mm, v(-0.7, -1.55) * mm, v(-0.97, -1.25) * mm, v(-1.04, -0.77) * mm]});
            skFitSpline(sketch, "E217", {"points": [v(-1.04, -0.77) * mm, v(-1.06, -0.65) * mm, v(-1.06, -0.24) * mm, v(-1.04, -0.11) * mm]});
            skFitSpline(sketch, "E218", {"points": [v(-1.04, -0.11) * mm, v(-1, 0.15) * mm, v(-0.91, 0.36) * mm, v(-0.76, 0.5) * mm]});
            skFitSpline(sketch, "E219", {"points": [v(-0.76, 0.5) * mm, v(-0.63, 0.62) * mm, v(-0.47, 0.7) * mm, v(-0.3, 0.73) * mm]});
            skFitSpline(sketch, "E220", {"points": [v(-0.3, 0.73) * mm, v(-0.18, 0.76) * mm, v(0.08, 0.75) * mm, v(0.19, 0.72) * mm]});
            skFitSpline(sketch, "E221", {"points": [v(0.19, 0.72) * mm, v(0.59, 0.61) * mm, v(0.82, 0.33) * mm, v(0.88, -0.12) * mm]});
            skFitSpline(sketch, "E222", {"points": [v(0.88, -0.12) * mm, v(0.9, -0.27) * mm, v(0.9, -0.65) * mm, v(0.87, -0.8) * mm]});
            skFitSpline(sketch, "E223", {"points": [v(0.87, -0.8) * mm, v(0.8, -1.22) * mm, v(0.57, -1.5) * mm, v(0.2, -1.6) * mm]});
            skFitSpline(sketch, "E224", {"points": [v(0.2, -1.6) * mm, v(0.1, -1.63) * mm, v(-0.17, -1.64) * mm, v(-0.27, -1.62) * mm]});
            skLineSegment(sketch, "E225", {"start": v(-5.58, -0.3) * mm, "end": v(-5.08, -0.3) * mm});
            skLineSegment(sketch, "E226", {"start": v(-5.08, -0.3) * mm, "end": v(-5.07, -0.28) * mm});
            skFitSpline(sketch, "E227", {"points": [v(0.13, -1.17) * mm, v(0.27, -1.1) * mm, v(0.35, -0.99) * mm, v(0.4, -0.8) * mm]});
            skFitSpline(sketch, "E228", {"points": [v(0.4, -0.8) * mm, v(0.4, -0.74) * mm, v(0.41, -0.67) * mm, v(0.41, -0.44) * mm]});
            skFitSpline(sketch, "E229", {"points": [v(0.41, -0.44) * mm, v(0.41, -0.13) * mm, v(0.4, -0.04) * mm, v(0.34, 0.09) * mm]});
            skFitSpline(sketch, "E230", {"points": [v(0.34, 0.09) * mm, v(0.25, 0.26) * mm, v(0.06, 0.36) * mm, v(-0.16, 0.32) * mm]});
            skFitSpline(sketch, "E231", {"points": [v(-0.16, 0.32) * mm, v(-0.37, 0.3) * mm, v(-0.5, 0.16) * mm, v(-0.55, -0.06) * mm]});
            skFitSpline(sketch, "E232", {"points": [v(-0.55, -0.06) * mm, v(-0.58, -0.19) * mm, v(-0.58, -0.7) * mm, v(-0.55, -0.81) * mm]});
            skFitSpline(sketch, "E233", {"points": [v(-0.55, -0.81) * mm, v(-0.51, -0.97) * mm, v(-0.46, -1.06) * mm, v(-0.36, -1.13) * mm]});
            skFitSpline(sketch, "E234", {"points": [v(-0.36, -1.13) * mm, v(-0.26, -1.2) * mm, v(-0.2, -1.21) * mm, v(-0.06, -1.2) * mm]});
            skFitSpline(sketch, "E235", {"points": [v(-0.06, -1.2) * mm, v(0.04, -1.2) * mm, v(0.06, -1.2) * mm, v(0.13, -1.17) * mm]});
            skFitSpline(sketch, "E236", {"points": [v(8.26, 0.75) * mm, v(8.39, 0.75) * mm, v(8.47, 0.75) * mm, v(8.5, 0.74) * mm]});
            skFitSpline(sketch, "E237", {"points": [v(8.5, 0.74) * mm, v(8.52, 0.72) * mm, v(8.55, 0.67) * mm, v(8.55, 0.62) * mm]});
            skLineSegment(sketch, "E238", {"start": v(8.03, -1.6) * mm, "end": v(8, -1.56) * mm});
            skLineSegment(sketch, "E239", {"start": v(8, -1.56) * mm, "end": v(8, -0.44) * mm});
            skLineSegment(sketch, "E240", {"start": v(8, -0.44) * mm, "end": v(8, 0.69) * mm});
            skLineSegment(sketch, "E241", {"start": v(8, 0.69) * mm, "end": v(8.03, 0.72) * mm});
            skLineSegment(sketch, "E242", {"start": v(8.03, 0.72) * mm, "end": v(8.06, 0.75) * mm});
            skLineSegment(sketch, "E243", {"start": v(8.06, 0.75) * mm, "end": v(8.26, 0.75) * mm});
            skFitSpline(sketch, "E244", {"points": [v(8.59, 0.62) * mm, v(8.65, 0.67) * mm, v(8.8, 0.74) * mm, v(8.9, 0.76) * mm]});
            skFitSpline(sketch, "E245", {"points": [v(8.9, 0.76) * mm, v(9, 0.78) * mm, v(9.2, 0.78) * mm, v(9.3, 0.76) * mm]});
            skFitSpline(sketch, "E246", {"points": [v(9.3, 0.76) * mm, v(9.44, 0.73) * mm, v(9.62, 0.62) * mm, v(9.66, 0.55) * mm]});
            skFitSpline(sketch, "E247", {"points": [v(9.66, 0.55) * mm, v(9.7, 0.5) * mm, v(9.67, 0.46) * mm, v(9.5, 0.3) * mm]});
            skFitSpline(sketch, "E248", {"points": [v(9.5, 0.3) * mm, v(9.35, 0.14) * mm, v(9.34, 0.13) * mm, v(9.3, 0.13) * mm]});
            skFitSpline(sketch, "E249", {"points": [v(9.3, 0.13) * mm, v(9.26, 0.13) * mm, v(9.24, 0.14) * mm, v(9.2, 0.17) * mm]});
            skFitSpline(sketch, "E250", {"points": [v(9.2, 0.17) * mm, v(9.12, 0.24) * mm, v(9.08, 0.25) * mm, v(8.96, 0.25) * mm]});
            skFitSpline(sketch, "E251", {"points": [v(8.96, 0.25) * mm, v(8.86, 0.25) * mm, v(8.84, 0.25) * mm, v(8.79, 0.22) * mm]});
            skFitSpline(sketch, "E252", {"points": [v(8.79, 0.22) * mm, v(8.7, 0.18) * mm, v(8.65, 0.12) * mm, v(8.6, 0.02) * mm]});
            skLineSegment(sketch, "E253", {"start": v(8.55, 0.62) * mm, "end": v(8.55, 0.6) * mm});
            skLineSegment(sketch, "E254", {"start": v(8.55, 0.6) * mm, "end": v(8.59, 0.62) * mm});
            skFitSpline(sketch, "E255", {"points": [v(-9.26, -1.6) * mm, v(-9.27, -1.57) * mm, v(-9.27, -1.44) * mm, v(-9.27, 0.03) * mm]});
            skFitSpline(sketch, "E256", {"points": [v(-9.27, 0.03) * mm, v(-9.27, 1.48) * mm, v(-9.27, 1.64) * mm, v(-9.26, 1.65) * mm]});
            skFitSpline(sketch, "E257", {"points": [v(-9.26, 1.65) * mm, v(-9.24, 1.67) * mm, v(-9.2, 1.67) * mm, v(-9.03, 1.67) * mm]});
            skLineSegment(sketch, "E258", {"start": v(8.6, 0.02) * mm, "end": v(8.57, -0.05) * mm});
            skLineSegment(sketch, "E259", {"start": v(8.57, -0.05) * mm, "end": v(8.56, -0.8) * mm});
            skLineSegment(sketch, "E260", {"start": v(8.56, -0.8) * mm, "end": v(8.56, -1.56) * mm});
            skLineSegment(sketch, "E261", {"start": v(8.56, -1.56) * mm, "end": v(8.52, -1.6) * mm});
            skLineSegment(sketch, "E262", {"start": v(8.52, -1.6) * mm, "end": v(8.49, -1.62) * mm});
            skLineSegment(sketch, "E263", {"start": v(8.49, -1.62) * mm, "end": v(8.27, -1.62) * mm});
            skLineSegment(sketch, "E264", {"start": v(8.27, -1.62) * mm, "end": v(8.06, -1.62) * mm});
            skLineSegment(sketch, "E265", {"start": v(8.06, -1.62) * mm, "end": v(8.03, -1.6) * mm});
            skFitSpline(sketch, "E266", {"points": [v(-8.19, 0.71) * mm, v(-7.38, -0.5) * mm, v(-7.4, -0.5) * mm, v(-7.37, -0.5) * mm]});
            skFitSpline(sketch, "E267", {"points": [v(-7.37, -0.5) * mm, v(-7.35, -0.5) * mm, v(-7.34, -0.5) * mm, v(-7.32, -0.49) * mm]});
            skFitSpline(sketch, "E268", {"points": [v(-7.32, -0.49) * mm, v(-7.3, -0.47) * mm, v(-7.3, -0.44) * mm, v(-7.3, 0.59) * mm]});
            skFitSpline(sketch, "E269", {"points": [v(-7.3, 0.59) * mm, v(-7.3, 1.4) * mm, v(-7.3, 1.65) * mm, v(-7.29, 1.66) * mm]});
            skFitSpline(sketch, "E270", {"points": [v(-7.29, 1.66) * mm, v(-7.28, 1.67) * mm, v(-7.21, 1.67) * mm, v(-7.05, 1.67) * mm]});
            skFitSpline(sketch, "E271", {"points": [v(-7.05, 1.67) * mm, v(-6.83, 1.67) * mm, v(-6.83, 1.67) * mm, v(-6.82, 1.64) * mm]});
            skFitSpline(sketch, "E272", {"points": [v(-6.82, 1.64) * mm, v(-6.8, 1.62) * mm, v(-6.8, 1.44) * mm, v(-6.8, 0.02) * mm]});
            skFitSpline(sketch, "E273", {"points": [v(-6.8, 0.02) * mm, v(-6.8, -1.55) * mm, v(-6.8, -1.58) * mm, v(-6.83, -1.6) * mm]});
            skFitSpline(sketch, "E274", {"points": [v(-6.83, -1.6) * mm, v(-6.85, -1.62) * mm, v(-7.23, -1.62) * mm, v(-7.26, -1.6) * mm]});
            skFitSpline(sketch, "E275", {"points": [v(-7.26, -1.6) * mm, v(-7.27, -1.6) * mm, v(-7.6, -1.1) * mm, v(-7.98, -0.52) * mm]});
            skFitSpline(sketch, "E276", {"points": [v(-7.98, -0.52) * mm, v(-8.36, 0.06) * mm, v(-8.69, 0.55) * mm, v(-8.7, 0.56) * mm]});
            skFitSpline(sketch, "E277", {"points": [v(-8.7, 0.56) * mm, v(-8.71, 0.57) * mm, v(-8.73, 0.57) * mm, v(-8.75, 0.56) * mm]});
            skLineSegment(sketch, "E278", {"start": v(-9.03, 1.67) * mm, "end": v(-8.81, 1.66) * mm});
            skLineSegment(sketch, "E279", {"start": v(-8.81, 1.66) * mm, "end": v(-8.19, 0.71) * mm});
            skFitSpline(sketch, "E280", {"points": [v(-8.77, -0.5) * mm, v(-8.77, -1.55) * mm, v(-8.77, -1.57) * mm, v(-8.8, -1.6) * mm]});
            skFitSpline(sketch, "E281", {"points": [v(-8.8, -1.6) * mm, v(-8.81, -1.61) * mm, v(-8.83, -1.61) * mm, v(-9.03, -1.61) * mm]});
            skFitSpline(sketch, "E282", {"points": [v(-9.03, -1.61) * mm, v(-9.22, -1.61) * mm, v(-9.24, -1.61) * mm, v(-9.26, -1.6) * mm]});
            skLineSegment(sketch, "E283", {"start": v(-8.75, 0.56) * mm, "end": v(-8.77, 0.55) * mm});
            skLineSegment(sketch, "E284", {"start": v(-8.77, 0.55) * mm, "end": v(-8.77, -0.5) * mm});
            skFitSpline(sketch, "E285", {"points": [v(-3.75, -1.6) * mm, v(-3.93, -1.56) * mm, v(-4.08, -1.45) * mm, v(-4.17, -1.28) * mm]});
            skFitSpline(sketch, "E286", {"points": [v(-4.17, -1.28) * mm, v(-4.24, -1.13) * mm, v(-4.24, -1.1) * mm, v(-4.24, -0.34) * mm]});
            skFitSpline(sketch, "E287", {"points": [v(-4.24, -0.34) * mm, v(-4.24, 0.19) * mm, v(-4.25, 0.34) * mm, v(-4.26, 0.35) * mm]});
            skFitSpline(sketch, "E288", {"points": [v(-4.26, 0.35) * mm, v(-4.27, 0.35) * mm, v(-4.32, 0.36) * mm, v(-4.38, 0.36) * mm]});
            skFitSpline(sketch, "E289", {"points": [v(-4.38, 0.36) * mm, v(-4.51, 0.37) * mm, v(-4.51, 0.37) * mm, v(-4.51, 0.54) * mm]});
            skFitSpline(sketch, "E290", {"points": [v(-4.51, 0.54) * mm, v(-4.51, 0.73) * mm, v(-4.51, 0.73) * mm, v(-4.37, 0.73) * mm]});
            skFitSpline(sketch, "E291", {"points": [v(-4.37, 0.73) * mm, v(-4.3, 0.73) * mm, v(-4.27, 0.73) * mm, v(-4.26, 0.74) * mm]});
            skFitSpline(sketch, "E292", {"points": [v(-4.26, 0.74) * mm, v(-4.25, 0.75) * mm, v(-4.24, 0.84) * mm, v(-4.24, 1.05) * mm]});
            skFitSpline(sketch, "E293", {"points": [v(-4.24, 1.05) * mm, v(-4.24, 1.23) * mm, v(-4.24, 1.35) * mm, v(-4.23, 1.37) * mm]});
            skFitSpline(sketch, "E294", {"points": [v(-4.23, 1.37) * mm, v(-4.22, 1.39) * mm, v(-4.2, 1.39) * mm, v(-4, 1.39) * mm]});
            skFitSpline(sketch, "E295", {"points": [v(-4, 1.39) * mm, v(-3.8, 1.39) * mm, v(-3.8, 1.39) * mm, v(-3.78, 1.36) * mm]});
            skFitSpline(sketch, "E296", {"points": [v(-3.78, 1.36) * mm, v(-3.76, 1.34) * mm, v(-3.76, 1.3) * mm, v(-3.76, 1.05) * mm]});
            skFitSpline(sketch, "E297", {"points": [v(-3.76, 1.05) * mm, v(-3.76, 0.84) * mm, v(-3.76, 0.75) * mm, v(-3.75, 0.74) * mm]});
            skFitSpline(sketch, "E298", {"points": [v(-3.75, 0.74) * mm, v(-3.74, 0.73) * mm, v(-3.68, 0.73) * mm, v(-3.54, 0.73) * mm]});
            skFitSpline(sketch, "E299", {"points": [v(-3.54, 0.73) * mm, v(-3.3, 0.73) * mm, v(-3.31, 0.74) * mm, v(-3.31, 0.55) * mm]});
            skFitSpline(sketch, "E300", {"points": [v(-3.31, 0.55) * mm, v(-3.31, 0.45) * mm, v(-3.32, 0.4) * mm, v(-3.33, 0.39) * mm]});
            skFitSpline(sketch, "E301", {"points": [v(-3.33, 0.39) * mm, v(-3.34, 0.37) * mm, v(-3.36, 0.36) * mm, v(-3.55, 0.36) * mm]});
            skFitSpline(sketch, "E302", {"points": [v(-3.76, -0.32) * mm, v(-3.76, -0.81) * mm, v(-3.76, -1.01) * mm, v(-3.75, -1.05) * mm]});
            skFitSpline(sketch, "E303", {"points": [v(-3.75, -1.05) * mm, v(-3.72, -1.16) * mm, v(-3.65, -1.2) * mm, v(-3.47, -1.2) * mm]});
            skFitSpline(sketch, "E304", {"points": [v(-3.47, -1.2) * mm, v(-3.37, -1.21) * mm, v(-3.34, -1.22) * mm, v(-3.33, -1.23) * mm]});
            skFitSpline(sketch, "E305", {"points": [v(-3.33, -1.23) * mm, v(-3.32, -1.24) * mm, v(-3.31, -1.3) * mm, v(-3.31, -1.4) * mm]});
            skFitSpline(sketch, "E306", {"points": [v(-3.31, -1.4) * mm, v(-3.31, -1.62) * mm, v(-3.3, -1.61) * mm, v(-3.51, -1.61) * mm]});
            skFitSpline(sketch, "E307", {"points": [v(-3.51, -1.61) * mm, v(-3.6, -1.61) * mm, v(-3.7, -1.6) * mm, v(-3.75, -1.6) * mm]});
            skLineSegment(sketch, "E308", {"start": v(-3.55, 0.36) * mm, "end": v(-3.76, 0.35) * mm});
            skLineSegment(sketch, "E309", {"start": v(-3.76, 0.35) * mm, "end": v(-3.76, -0.32) * mm});
            skFitSpline(sketch, "E310", {"points": [v(1.16, -1.6) * mm, v(1.14, -1.58) * mm, v(1.14, -1.55) * mm, v(1.14, -0.45) * mm]});
            skFitSpline(sketch, "E311", {"points": [v(1.14, -0.45) * mm, v(1.13, 0.67) * mm, v(1.13, 0.68) * mm, v(1.16, 0.7) * mm]});
            skFitSpline(sketch, "E312", {"points": [v(1.16, 0.7) * mm, v(1.18, 0.73) * mm, v(1.2, 0.73) * mm, v(1.38, 0.73) * mm]});
            skFitSpline(sketch, "E313", {"points": [v(1.38, 0.73) * mm, v(1.58, 0.73) * mm, v(1.58, 0.73) * mm, v(1.6, 0.7) * mm]});
            skFitSpline(sketch, "E314", {"points": [v(1.6, 0.7) * mm, v(1.61, 0.68) * mm, v(1.62, 0.55) * mm, v(1.62, -0.44) * mm]});
            skFitSpline(sketch, "E315", {"points": [v(1.62, -0.44) * mm, v(1.62, -1.55) * mm, v(1.62, -1.57) * mm, v(1.6, -1.6) * mm]});
            skFitSpline(sketch, "E316", {"points": [v(1.6, -1.6) * mm, v(1.57, -1.61) * mm, v(1.56, -1.61) * mm, v(1.38, -1.61) * mm]});
            skFitSpline(sketch, "E317", {"points": [v(1.38, -1.61) * mm, v(1.23, -1.61) * mm, v(1.18, -1.6) * mm, v(1.16, -1.6) * mm]});
            skFitSpline(sketch, "E318", {"points": [v(2, -1.6) * mm, v(1.98, -1.6) * mm, v(1.98, -1.52) * mm, v(1.98, -0.44) * mm]});
            skFitSpline(sketch, "E319", {"points": [v(1.98, -0.44) * mm, v(1.98, 0.68) * mm, v(1.98, 0.7) * mm, v(2, 0.72) * mm]});
            skFitSpline(sketch, "E320", {"points": [v(2, 0.72) * mm, v(2, 0.72) * mm, v(2.1, 0.73) * mm, v(2.2, 0.73) * mm]});
            skFitSpline(sketch, "E321", {"points": [v(2.2, 0.73) * mm, v(2.42, 0.73) * mm, v(2.43, 0.72) * mm, v(2.43, 0.64) * mm]});
            skFitSpline(sketch, "E322", {"points": [v(2.43, 0.64) * mm, v(2.43, 0.6) * mm, v(2.46, 0.56) * mm, v(2.49, 0.56) * mm]});
            skFitSpline(sketch, "E323", {"points": [v(2.49, 0.56) * mm, v(2.5, 0.56) * mm, v(2.52, 0.58) * mm, v(2.54, 0.6) * mm]});
            skFitSpline(sketch, "E324", {"points": [v(2.54, 0.6) * mm, v(2.62, 0.65) * mm, v(2.75, 0.7) * mm, v(2.85, 0.73) * mm]});
            skFitSpline(sketch, "E325", {"points": [v(2.85, 0.73) * mm, v(2.99, 0.76) * mm, v(3.2, 0.76) * mm, v(3.34, 0.71) * mm]});
            skFitSpline(sketch, "E326", {"points": [v(3.34, 0.71) * mm, v(3.64, 0.62) * mm, v(3.82, 0.38) * mm, v(3.86, 0.05) * mm]});
            skFitSpline(sketch, "E327", {"points": [v(3.86, 0.05) * mm, v(3.86, 0) * mm, v(3.87, -0.38) * mm, v(3.87, -0.8) * mm]});
            skFitSpline(sketch, "E328", {"points": [v(3.87, -0.8) * mm, v(3.87, -1.55) * mm, v(3.87, -1.57) * mm, v(3.85, -1.6) * mm]});
            skFitSpline(sketch, "E329", {"points": [v(3.85, -1.6) * mm, v(3.83, -1.61) * mm, v(3.8, -1.61) * mm, v(3.63, -1.61) * mm]});
            skFitSpline(sketch, "E330", {"points": [v(3.63, -1.61) * mm, v(3.5, -1.61) * mm, v(3.43, -1.6) * mm, v(3.42, -1.6) * mm]});
            skFitSpline(sketch, "E331", {"points": [v(3.42, -1.6) * mm, v(3.4, -1.59) * mm, v(3.4, -1.52) * mm, v(3.4, -0.83) * mm]});
            skFitSpline(sketch, "E332", {"points": [v(3.4, -0.83) * mm, v(3.4, -0.16) * mm, v(3.39, -0.06) * mm, v(3.37, 0) * mm]});
            skFitSpline(sketch, "E333", {"points": [v(3.37, 0) * mm, v(3.32, 0.19) * mm, v(3.2, 0.3) * mm, v(3, 0.32) * mm]});
            skFitSpline(sketch, "E334", {"points": [v(3, 0.32) * mm, v(2.74, 0.36) * mm, v(2.52, 0.22) * mm, v(2.46, -0.02) * mm]});
            skFitSpline(sketch, "E335", {"points": [v(2.46, -0.02) * mm, v(2.45, -0.08) * mm, v(2.45, -0.21) * mm, v(2.45, -0.83) * mm]});
            skFitSpline(sketch, "E336", {"points": [v(2.45, -0.83) * mm, v(2.45, -1.55) * mm, v(2.45, -1.57) * mm, v(2.42, -1.6) * mm]});
            skFitSpline(sketch, "E337", {"points": [v(2.42, -1.6) * mm, v(2.4, -1.61) * mm, v(2.39, -1.61) * mm, v(2.2, -1.61) * mm]});
            skFitSpline(sketch, "E338", {"points": [v(2.2, -1.61) * mm, v(2.1, -1.61) * mm, v(2, -1.6) * mm, v(2, -1.6) * mm]});
            skFitSpline(sketch, "E339", {"points": [v(4.77, -1.6) * mm, v(4.52, -1.56) * mm, v(4.35, -1.4) * mm, v(4.28, -1.15) * mm]});
            skFitSpline(sketch, "E340", {"points": [v(4.28, -1.15) * mm, v(4.26, -1.09) * mm, v(4.26, -1) * mm, v(4.25, -0.38) * mm]});
            skFitSpline(sketch, "E341", {"points": [v(4.25, -0.38) * mm, v(4.25, 0.1) * mm, v(4.24, 0.33) * mm, v(4.24, 0.34) * mm]});
            skFitSpline(sketch, "E342", {"points": [v(4.24, 0.34) * mm, v(4.23, 0.35) * mm, v(4.2, 0.36) * mm, v(4.13, 0.36) * mm]});
            skFitSpline(sketch, "E343", {"points": [v(4.13, 0.36) * mm, v(4, 0.36) * mm, v(4, 0.36) * mm, v(4, 0.55) * mm]});
            skFitSpline(sketch, "E344", {"points": [v(4, 0.55) * mm, v(4, 0.73) * mm, v(3.99, 0.73) * mm, v(4.13, 0.73) * mm]});
            skFitSpline(sketch, "E345", {"points": [v(4.13, 0.73) * mm, v(4.2, 0.73) * mm, v(4.23, 0.73) * mm, v(4.24, 0.74) * mm]});
            skFitSpline(sketch, "E346", {"points": [v(4.24, 0.74) * mm, v(4.24, 0.75) * mm, v(4.25, 0.87) * mm, v(4.25, 1.06) * mm]});
            skFitSpline(sketch, "E347", {"points": [v(4.25, 1.06) * mm, v(4.26, 1.32) * mm, v(4.26, 1.37) * mm, v(4.27, 1.38) * mm]});
            skFitSpline(sketch, "E348", {"points": [v(4.27, 1.38) * mm, v(4.28, 1.38) * mm, v(4.38, 1.39) * mm, v(4.5, 1.39) * mm]});
            skFitSpline(sketch, "E349", {"points": [v(4.5, 1.39) * mm, v(4.7, 1.39) * mm, v(4.7, 1.39) * mm, v(4.72, 1.37) * mm]});
            skFitSpline(sketch, "E350", {"points": [v(4.72, 1.37) * mm, v(4.73, 1.35) * mm, v(4.73, 1.23) * mm, v(4.73, 1.05) * mm]});
            skFitSpline(sketch, "E351", {"points": [v(4.73, 1.05) * mm, v(4.73, 0.84) * mm, v(4.74, 0.75) * mm, v(4.75, 0.74) * mm]});
            skFitSpline(sketch, "E352", {"points": [v(4.75, 0.74) * mm, v(4.75, 0.73) * mm, v(4.82, 0.73) * mm, v(4.95, 0.73) * mm]});
            skFitSpline(sketch, "E353", {"points": [v(4.95, 0.73) * mm, v(5.2, 0.73) * mm, v(5.18, 0.74) * mm, v(5.18, 0.54) * mm]});
            skFitSpline(sketch, "E354", {"points": [v(5.18, 0.54) * mm, v(5.18, 0.35) * mm, v(5.2, 0.36) * mm, v(4.94, 0.36) * mm]});
            skFitSpline(sketch, "E355", {"points": [v(4.94, 0.36) * mm, v(4.81, 0.36) * mm, v(4.75, 0.36) * mm, v(4.75, 0.35) * mm]});
            skFitSpline(sketch, "E356", {"points": [v(4.75, 0.35) * mm, v(4.73, 0.33) * mm, v(4.73, -0.98) * mm, v(4.74, -1.04) * mm]});
            skFitSpline(sketch, "E357", {"points": [v(4.74, -1.04) * mm, v(4.76, -1.1) * mm, v(4.82, -1.16) * mm, v(4.87, -1.18) * mm]});
            skFitSpline(sketch, "E358", {"points": [v(4.87, -1.18) * mm, v(4.89, -1.2) * mm, v(4.96, -1.2) * mm, v(5.03, -1.2) * mm]});
            skFitSpline(sketch, "E359", {"points": [v(5.03, -1.2) * mm, v(5.12, -1.21) * mm, v(5.16, -1.22) * mm, v(5.17, -1.23) * mm]});
            skFitSpline(sketch, "E360", {"points": [v(5.17, -1.23) * mm, v(5.18, -1.24) * mm, v(5.18, -1.3) * mm, v(5.18, -1.41) * mm]});
            skFitSpline(sketch, "E361", {"points": [v(5.18, -1.41) * mm, v(5.18, -1.62) * mm, v(5.2, -1.61) * mm, v(4.98, -1.61) * mm]});
            skFitSpline(sketch, "E362", {"points": [v(4.98, -1.61) * mm, v(4.9, -1.61) * mm, v(4.8, -1.6) * mm, v(4.77, -1.6) * mm]});
            skFitSpline(sketch, "E363", {"points": [v(-12.95, -1.04) * mm, v(-13.02, -1.01) * mm, v(-13.03, -1.01) * mm, v(-13.34, -0.84) * mm]});
            skFitSpline(sketch, "E364", {"points": [v(-13.34, -0.84) * mm, v(-13.63, -0.67) * mm, v(-13.7, -0.62) * mm, v(-13.75, -0.5) * mm]});
            skFitSpline(sketch, "E365", {"points": [v(-13.75, -0.5) * mm, v(-13.8, -0.4) * mm, v(-13.8, -0.34) * mm, v(-13.8, 0.07) * mm]});
            skFitSpline(sketch, "E366", {"points": [v(-13.76, 0.49) * mm, v(-13.7, 0.61) * mm, v(-13.63, 0.67) * mm, v(-13.31, 0.85) * mm]});
            skFitSpline(sketch, "E367", {"points": [v(-13.31, 0.85) * mm, v(-13.16, 0.94) * mm, v(-13.01, 1.02) * mm, v(-12.99, 1.02) * mm]});
            skFitSpline(sketch, "E368", {"points": [v(-12.99, 1.02) * mm, v(-12.87, 1.07) * mm, v(-12.73, 1.06) * mm, v(-12.61, 1) * mm]});
            skFitSpline(sketch, "E369", {"points": [v(-12.61, 1) * mm, v(-12.58, 0.98) * mm, v(-12.44, 0.9) * mm, v(-12.3, 0.83) * mm]});
            skFitSpline(sketch, "E370", {"points": [v(-12.3, 0.83) * mm, v(-11.87, 0.57) * mm, v(-11.85, 0.54) * mm, v(-11.85, 0) * mm]});
            skFitSpline(sketch, "E371", {"points": [v(-11.85, 0) * mm, v(-11.85, -0.34) * mm, v(-11.86, -0.4) * mm, v(-11.9, -0.5) * mm]});
            skFitSpline(sketch, "E372", {"points": [v(-11.9, -0.5) * mm, v(-11.96, -0.61) * mm, v(-12.04, -0.67) * mm, v(-12.34, -0.85) * mm]});
            skFitSpline(sketch, "E373", {"points": [v(-12.34, -0.85) * mm, v(-12.5, -0.93) * mm, v(-12.64, -1.01) * mm, v(-12.68, -1.02) * mm]});
            skFitSpline(sketch, "E374", {"points": [v(-12.68, -1.02) * mm, v(-12.75, -1.05) * mm, v(-12.88, -1.06) * mm, v(-12.95, -1.04) * mm]});
            skLineSegment(sketch, "E375", {"start": v(-13.8, 0.07) * mm, "end": v(-13.8, 0.4) * mm});
            skLineSegment(sketch, "E376", {"start": v(-13.8, 0.4) * mm, "end": v(-13.76, 0.49) * mm});
            skFitSpline(sketch, "E377", {"points": [v(1.14, 1.2) * mm, v(1.13, 1.22) * mm, v(1.12, 1.32) * mm, v(1.12, 1.44) * mm]});
            skFitSpline(sketch, "E378", {"points": [v(1.12, 1.44) * mm, v(1.12, 1.61) * mm, v(1.13, 1.65) * mm, v(1.14, 1.66) * mm]});
            skFitSpline(sketch, "E379", {"points": [v(1.14, 1.66) * mm, v(1.16, 1.68) * mm, v(1.2, 1.68) * mm, v(1.38, 1.68) * mm]});
            skFitSpline(sketch, "E380", {"points": [v(1.38, 1.68) * mm, v(1.6, 1.68) * mm, v(1.6, 1.68) * mm, v(1.62, 1.66) * mm]});
            skFitSpline(sketch, "E381", {"points": [v(1.62, 1.66) * mm, v(1.62, 1.65) * mm, v(1.63, 1.55) * mm, v(1.63, 1.43) * mm]});
            skFitSpline(sketch, "E382", {"points": [v(1.63, 1.43) * mm, v(1.63, 1.32) * mm, v(1.62, 1.22) * mm, v(1.62, 1.2) * mm]});
            skFitSpline(sketch, "E383", {"points": [v(1.62, 1.2) * mm, v(1.6, 1.19) * mm, v(1.6, 1.19) * mm, v(1.38, 1.19) * mm]});
            skFitSpline(sketch, "E384", {"points": [v(1.38, 1.19) * mm, v(1.16, 1.19) * mm, v(1.15, 1.19) * mm, v(1.14, 1.2) * mm]});
            skSolve(sketch);
        }
        {
            var Q0;
            Q0 = qSketchRegion(id + "F0", true);
            var Q1;
            Q1 = qSketchRegion(id + "F2", true);
            extrude(context, id + "F1", {"entities" : qUnion([Q0, Q1]), "depth" : 2 * mm, "offsetDistance" : 25 * mm});
        }
        {
            var Q0;
            Q0=makeQuery(id+"F1.opExtrude","CAP_FACE",FACE,{"disambiguationData":[OSD([sQuery(id+"F0.wireOp",EDGE,"E73"),sQuery(id+"F0.wireOp",EDGE,"E74"),sQuery(id+"F0.wireOp",EDGE,"E75"),sQuery(id+"F0.wireOp",EDGE,"E76"),sQuery(id+"F0.wireOp",EDGE,"E77"),sQuery(id+"F0.wireOp",EDGE,"E78"),sQuery(id+"F0.wireOp",EDGE,"E79"),sQuery(id+"F0.wireOp",EDGE,"E80"),sQuery(id+"F0.wireOp",EDGE,"E81"),sQuery(id+"F0.wireOp",EDGE,"E82"),sQuery(id+"F0.wireOp",EDGE,"E83"),sQuery(id+"F0.wireOp",EDGE,"E84"),sQuery(id+"F0.wireOp",EDGE,"E85"),sQuery(id+"F0.wireOp",EDGE,"E86"),sQuery(id+"F0.wireOp",EDGE,"E87"),sQuery(id+"F0.wireOp",EDGE,"E88"),sQuery(id+"F0.wireOp",EDGE,"E89"),sQuery(id+"F0.wireOp",EDGE,"E90"),sQuery(id+"F0.wireOp",EDGE,"E91"),sQuery(id+"F0.wireOp",EDGE,"E92"),sQuery(id+"F0.wireOp",EDGE,"E93"),sQuery(id+"F0.wireOp",EDGE,"E94"),sQuery(id+"F0.wireOp",EDGE,"E95"),sQuery(id+"F0.wireOp",EDGE,"E96"),sQuery(id+"F0.wireOp",EDGE,"E97"),sQuery(id+"F0.wireOp",EDGE,"E98"),sQuery(id+"F0.wireOp",EDGE,"E99"),sQuery(id+"F0.wireOp",EDGE,"E100")])],"isStart":true});
            var sketch = newSketch(context, id + "F2", { "sketchPlane" : qUnion([Q0])});
            skLineSegment(sketch, "E385.bottom", {"start": v(18.86, -5.4) * mm, "end": v(-20.87, -5.4) * mm});
            skLineSegment(sketch, "E385.top", {"start": v(18.86, 5.4) * mm, "end": v(-20.87, 5.4) * mm});
            skLineSegment(sketch, "E385.left", {"start": v(18.86, -5.4) * mm, "end": v(18.86, 5.4) * mm});
            skLineSegment(sketch, "E385.right", {"start": v(-20.87, -5.4) * mm, "end": v(-20.87, 5.4) * mm});
            skSolve(sketch);
        }
        {
            var Q0;
            Q0 = qSketchRegion(id + "F2", true);
            extrude(context, id + "F3", {"entities" : qUnion([Q0]), "depth" : 3 * mm, "offsetDistance" : 25 * mm});
        }
        {
            var Q0;
            Q0=makeQuery(id+"F3.opExtrude","SWEPT_EDGE",EDGE,{"disambiguationData":[OSD([sQuery(id+"F2.wireOp",EDGE,"E385.bottom"),sQuery(id+"F2.wireOp",EDGE,"E385.right")])]});
            var Q1;
            Q1=makeQuery(id+"F3.opExtrude","SWEPT_EDGE",EDGE,{"disambiguationData":[OSD([sQuery(id+"F2.wireOp",EDGE,"E385.top"),sQuery(id+"F2.wireOp",EDGE,"E385.right")])]});
            var Q2;
            Q2=makeQuery(id+"F3.opExtrude","SWEPT_EDGE",EDGE,{"disambiguationData":[OSD([sQuery(id+"F2.wireOp",EDGE,"E385.top"),sQuery(id+"F2.wireOp",EDGE,"E385.left")])]});
            var Q3;
            Q3=makeQuery(id+"F3.opExtrude","SWEPT_EDGE",EDGE,{"disambiguationData":[OSD([sQuery(id+"F2.wireOp",EDGE,"E385.bottom"),sQuery(id+"F2.wireOp",EDGE,"E385.left")])]});
            fillet(context, id + "F4", {"entities" : qUnion([Q0, Q1, Q2, Q3]), "radius" : 5 * mm, "tangentPropagation" : true, "allowEdgeOverflow" : false});
        }
        {
            var Q0;
            Q0=makeQuery(id+"F3.opExtrude","CAP_FACE",FACE,{"disambiguationData":[OSD([sQuery(id+"F2.wireOp",EDGE,"E385.bottom"),sQuery(id+"F2.wireOp",EDGE,"E385.top"),sQuery(id+"F2.wireOp",EDGE,"E385.left"),sQuery(id+"F2.wireOp",EDGE,"E385.right")])],"isStart":true});
            var sketch = newSketch(context, id + "F5", { "sketchPlane" : qUnion([Q0])});
            skPoint(sketch, "E386", {"position": v(-17.87, 0) * mm});
            skLineSegment(sketch, "E387", {"start": v(-17.87, 5.4) * mm, "end": v(-17.87, -5.4) * mm});
            skSolve(sketch);
        }
        {
            var Q0;
            Q0=sQuery(id+"F5.wireOp",VERTEX,"E386");
            var Q1;
            Q1=makeQuery(id+"F3.opExtrude","SWEPT_BODY",BODY,{"disambiguationData":[OSD([sQuery(id+"F2.wireOp",EDGE,"E385.bottom"),sQuery(id+"F2.wireOp",EDGE,"E385.top"),sQuery(id+"F2.wireOp",EDGE,"E385.left"),sQuery(id+"F2.wireOp",EDGE,"E385.right")])]});
            hole(context, id + "F6", {"style" : HoleStyle.SIMPLE, "endStyle" : HoleEndStyle.THROUGH, "holeDiameter" : 3 * mm, "majorDiameter" : 5 * mm, "isTappedThrough" : true, "tappedDepth" : 12 * mm, "tapClearance" : 3, "locations" : qUnion([Q0]), "scope" : qUnion([Q1])});
        }
    });
